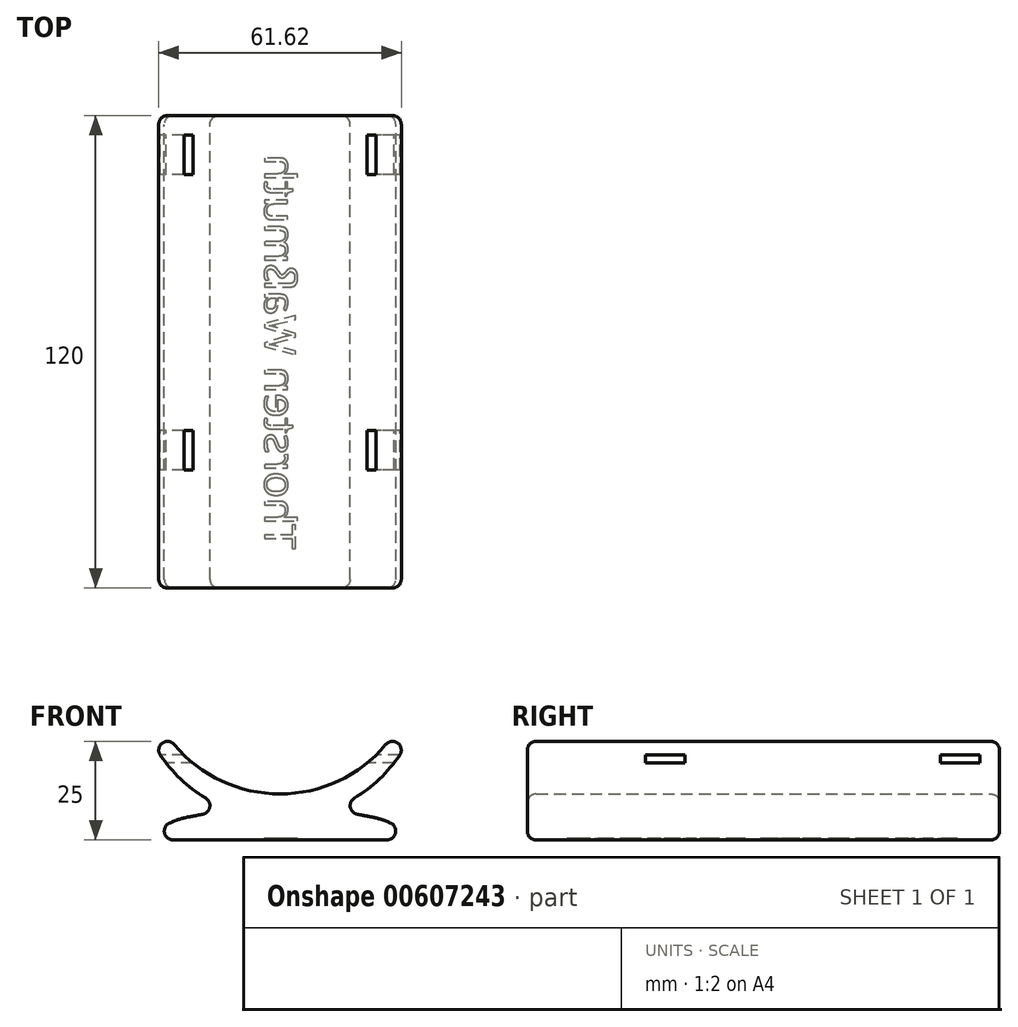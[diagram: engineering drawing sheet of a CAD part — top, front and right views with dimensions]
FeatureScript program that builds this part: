
annotation { "Feature Type Name" : "Feature", "Feature Type Description" : "" }
export const myFeature = defineFeature(function(context is Context, id is Id, definition is map)
    precondition{}
    {
        {
            var Q0;
            Q0=qCreatedBy(makeId("Front.planeOp"),FACE);
            var sketch = newSketch(context, id + "F0", { "sketchPlane" : qUnion([Q0])});
            skLineSegment(sketch, "E0", {"start": v(-32.5, 0) * mm, "end": v(32.5, 0) * mm});
            skLineSegment(sketch, "E1", {"start": v(32.5, 25) * mm, "end": v(27.5, 25) * mm});
            skLineSegment(sketch, "E2", {"start": v(-32.5, 25) * mm, "end": v(-27.5, 25) * mm});
            skArc(sketch, "E3", {"start": v(-27.5, 25) * mm, "mid": v(0, 11.65) * mm, "end": v(27.5, 25) * mm});
            skArc(sketch, "E4", {"start": v(-32.5, 25) * mm, "mid": v(0, 5.37) * mm, "end": v(32.5, 25) * mm});
            skFitSpline(sketch, "E5", {"points": [v(-32.5, 0) * mm, v(-24.4, 5.56) * mm, v(-15.17, 8.65) * mm], "startDerivative": vector(7.79, 17.92) * mm, "endDerivative": vector(11.83, 13.14) * mm});
            skFitSpline(sketch, "E6.MirrorCS", {"points": [v(32.5, 0) * mm, v(24.4, 5.56) * mm, v(15.17, 8.65) * mm], "startDerivative": vector(-7.79, 17.92) * mm, "endDerivative": vector(-11.83, 13.14) * mm});
            skLineSegment(sketch, "E7", {"start": v(15.17, 8.65) * mm, "end": v(-15.17, 8.65) * mm});
            skSolve(sketch);
        }
        {
            var Q0;
            Q0 = qSketchRegion(id + "F0", true);
            extrude(context, id + "F1", {"entities" : qUnion([Q0]), "depth" : 60 * mm, "offsetDistance" : 25 * mm, "hasSecondDirection" : true, "secondDirectionOppositeDirection" : true, "secondDirectionDepth" : 60 * mm});
        }
        {
            var Q0;
            Q0=makeQuery(id+"F1.opExtrude","CAP_EDGE",EDGE,{"disambiguationData":[OSD([sQuery(id+"F0.wireOp",EDGE,"E1")])],"isStart":false});
            var Q1;
            Q1=makeQuery(id+"F1.opExtrude","CAP_EDGE",EDGE,{"disambiguationData":[OSD([sQuery(id+"F0.wireOp",EDGE,"E2")])],"isStart":false});
            var Q2;
            Q2=makeQuery(id+"F1.opExtrude","CAP_EDGE",EDGE,{"disambiguationData":[OSD([sQuery(id+"F0.wireOp",EDGE,"6ac28e1d-b41e-4c74-82fc-2945b80d29a40.MirrorCS")])],"isStart":false});
            var Q3;
            Q3=makeQuery(id+"F1.opExtrude","CAP_EDGE",EDGE,{"disambiguationData":[OSD([sQuery(id+"F0.wireOp",EDGE,"E3")])],"isStart":false});
            var Q4;
            Q4=makeQuery(id+"F1.opExtrude","SWEPT_FACE",FACE,{"disambiguationData":[OSD([sQuery(id+"F0.wireOp",EDGE,"UTH5XIte-BIU0-CYo0-HlKk-KP9v13hWMDFO")])]});
            var Q5;
            Q5=makeQuery(id+"F1.opExtrude","CAP_EDGE",EDGE,{"disambiguationData":[OSD([sQuery(id+"F0.wireOp",EDGE,"E0")])],"isStart":false});
            var Q6;
            Q6=makeQuery(id+"F1.opExtrude","SWEPT_EDGE",EDGE,{"disambiguationData":[OSD([sQuery(id+"F0.wireOp",EDGE,"E2"),sQuery(id+"F0.wireOp",EDGE,"E3")])]});
            var Q7;
            Q7=makeQuery(id+"F1.opExtrude","SWEPT_EDGE",EDGE,{"disambiguationData":[OSD([sQuery(id+"F0.wireOp",EDGE,"E2"),sQuery(id+"F0.wireOp",EDGE,"6ac28e1d-b41e-4c74-82fc-2945b80d29a40.MirrorCS")])]});
            var Q8;
            Q8=makeQuery(id+"F1.opExtrude","CAP_EDGE",EDGE,{"disambiguationData":[OSD([sQuery(id+"F0.wireOp",EDGE,"6ac28e1d-b41e-4c74-82fc-2945b80d29a40.MirrorCS")])],"isStart":true});
            var Q9;
            Q9=makeQuery(id+"F1.opExtrude","CAP_EDGE",EDGE,{"disambiguationData":[OSD([sQuery(id+"F0.wireOp",EDGE,"E3")])],"isStart":true});
            var Q10;
            Q10=makeQuery(id+"F1.opExtrude","CAP_EDGE",EDGE,{"disambiguationData":[OSD([sQuery(id+"F0.wireOp",EDGE,"E1")])],"isStart":true});
            var Q11;
            Q11=makeQuery(id+"F1.opExtrude","CAP_EDGE",EDGE,{"disambiguationData":[OSD([sQuery(id+"F0.wireOp",EDGE,"E2")])],"isStart":true});
            var Q12;
            Q12=makeQuery(id+"F1.opExtrude","CAP_EDGE",EDGE,{"disambiguationData":[OSD([sQuery(id+"F0.wireOp",EDGE,"E0")])],"isStart":true});
            var Q13;
            Q13=makeQuery(id+"F1.opExtrude","SWEPT_EDGE",EDGE,{"disambiguationData":[OSD([sQuery(id+"F0.wireOp",EDGE,"E0"),sQuery(id+"F0.wireOp",EDGE,"6ac28e1d-b41e-4c74-82fc-2945b80d29a40.MirrorCS")])]});
            var Q14;
            Q14=makeQuery(id+"F1.opExtrude","SWEPT_FACE",FACE,{"disambiguationData":[OSD([sQuery(id+"F0.wireOp",EDGE,"E3")])]});
            var Q15;
            {var subQ0=sQuery(id+"F0.wireOp",EDGE,"E4");Q15=makeQuery(id+"F1.opExtrude","CAP_EDGE",EDGE,{"disambiguationData":[OSD([subQ0]),TDD([makeQuery(id+"F0.imprint","IMPRINT",EDGE,{"disambiguationData":[TD([[makeQuery(id+"F0.imprint","INTERSECT",VERTEX,{"derivedFrom":[sQuery(id+"F0.wireOp",EDGE,"E1"),subQ0]}),1.0]])],"derivedFrom":subQ0})])],"isStart":true});}
            var Q16;
            Q16=makeQuery(id+"F1.opExtrude","SWEPT_EDGE",EDGE,{"disambiguationData":[OSD([sQuery(id+"F0.wireOp",EDGE,"E1"),sQuery(id+"F0.wireOp",EDGE,"E4")])]});
            var Q17;
            Q17=makeQuery(id+"F1.opExtrude","CAP_EDGE",EDGE,{"disambiguationData":[OSD([sQuery(id+"F0.wireOp",EDGE,"E6.MirrorCS")])],"isStart":true});
            var Q18;
            {var subQ0=sQuery(id+"F0.wireOp",EDGE,"E4");Q18=makeQuery(id+"F1.opExtrude","CAP_EDGE",EDGE,{"disambiguationData":[OSD([subQ0]),TDD([makeQuery(id+"F0.imprint","IMPRINT",EDGE,{"disambiguationData":[TD([[makeQuery(id+"F0.imprint","INTERSECT",VERTEX,{"derivedFrom":[sQuery(id+"F0.wireOp",EDGE,"E2"),subQ0]}),-1.0]])],"derivedFrom":subQ0})])],"isStart":true});}
            var Q19;
            Q19=makeQuery(id+"F1.opExtrude","CAP_EDGE",EDGE,{"disambiguationData":[OSD([sQuery(id+"F0.wireOp",EDGE,"E5")])],"isStart":true});
            var Q20;
            {var subQ0=sQuery(id+"F0.wireOp",EDGE,"E4");Q20=makeQuery(id+"F1.opExtrude","CAP_EDGE",EDGE,{"disambiguationData":[OSD([subQ0]),TDD([makeQuery(id+"F0.imprint","IMPRINT",EDGE,{"disambiguationData":[TD([[makeQuery(id+"F0.imprint","INTERSECT",VERTEX,{"derivedFrom":[sQuery(id+"F0.wireOp",EDGE,"E2"),subQ0]}),-1.0]])],"derivedFrom":subQ0})])],"isStart":false});}
            var Q21;
            Q21=makeQuery(id+"F1.opExtrude","CAP_EDGE",EDGE,{"disambiguationData":[OSD([sQuery(id+"F0.wireOp",EDGE,"E5")])],"isStart":false});
            var Q22;
            Q22=makeQuery(id+"F1.opExtrude","CAP_EDGE",EDGE,{"disambiguationData":[OSD([sQuery(id+"F0.wireOp",EDGE,"E6.MirrorCS")])],"isStart":false});
            var Q23;
            {var subQ0=sQuery(id+"F0.wireOp",EDGE,"E4");Q23=makeQuery(id+"F1.opExtrude","CAP_EDGE",EDGE,{"disambiguationData":[OSD([subQ0]),TDD([makeQuery(id+"F0.imprint","IMPRINT",EDGE,{"disambiguationData":[TD([[makeQuery(id+"F0.imprint","INTERSECT",VERTEX,{"derivedFrom":[sQuery(id+"F0.wireOp",EDGE,"E1"),subQ0]}),1.0]])],"derivedFrom":subQ0})])],"isStart":false});}
            var Q24;
            Q24=makeQuery(id+"F1.opExtrude","SWEPT_EDGE",EDGE,{"disambiguationData":[OSD([sQuery(id+"F0.wireOp",EDGE,"E4"),sQuery(id+"F0.wireOp",EDGE,"E6.MirrorCS")])]});
            var Q25;
            Q25=makeQuery(id+"F1.opExtrude","SWEPT_EDGE",EDGE,{"disambiguationData":[OSD([sQuery(id+"F0.wireOp",EDGE,"E4"),sQuery(id+"F0.wireOp",EDGE,"E5")])]});
            fillet(context, id + "F2", {"entities" : qUnion([Q0, Q1, Q2, Q3, Q4, Q5, Q6, Q7, Q8, Q9, Q10, Q11, Q12, Q13, Q14, Q15, Q16, Q17, Q18, Q19, Q20, Q21, Q22, Q23, Q24, Q25]), "radius" : 2.22 * mm, "tangentPropagation" : true, "allowEdgeOverflow" : false});
        }
        {
            var Q0;
            Q0=qCreatedBy(makeId("Right.planeOp"),FACE);
            var sketch = newSketch(context, id + "F3", { "sketchPlane" : qUnion([Q0])});
            skLineSegment(sketch, "E8.bottom", {"start": v(45, 21.54) * mm, "end": v(55, 21.54) * mm});
            skLineSegment(sketch, "E8.top", {"start": v(45, 19.54) * mm, "end": v(55, 19.54) * mm});
            skLineSegment(sketch, "E8.left", {"start": v(45, 21.54) * mm, "end": v(45, 19.54) * mm});
            skLineSegment(sketch, "E8.right", {"start": v(55, 21.54) * mm, "end": v(55, 19.54) * mm});
            skLineSegment(sketch, "E9.bottom", {"start": v(-30, 21.54) * mm, "end": v(-20, 21.54) * mm});
            skLineSegment(sketch, "E9.top", {"start": v(-30, 19.54) * mm, "end": v(-20, 19.54) * mm});
            skLineSegment(sketch, "E9.left", {"start": v(-30, 21.54) * mm, "end": v(-30, 19.54) * mm});
            skLineSegment(sketch, "E9.right", {"start": v(-20, 21.54) * mm, "end": v(-20, 19.54) * mm});
            skSolve(sketch);
        }
        {
            var Q0;
            Q0=qSketchRegion(id+"F3",true);
            extrude(context, id + "F4", {"entities" : qUnion([Q0]), "operationType" : NewBodyOperationType.REMOVE, "endBound" : BoundingType.THROUGH_ALL, "depth" : 25 * mm, "offsetDistance" : 25 * mm, "hasSecondDirection" : true, "secondDirectionBound" : SecondDirectionBoundingType.THROUGH_ALL, "secondDirectionOppositeDirection" : true, "secondDirectionDepth" : 25 * mm});
        }
        {
            var Q0;
            Q0=makeQuery(id+"F1.opExtrude","SWEPT_FACE",FACE,{"disambiguationData":[OSD([sQuery(id+"F0.wireOp",EDGE,"E0")])]});
            var sketch = newSketch(context, id + "F5", { "sketchPlane" : qUnion([Q0])});
            skText(sketch, "E10", { "text": "Thorsten Waßmuth", "fontName": "OpenSans-Regular.ttf"});
            const initialGuessF5  = {"E10": [-0.00398, 0.05, 0, -1, 0.00796]};
            skSetInitialGuess(sketch, initialGuessF5);
            skSolve(sketch);
        }
        {
            var Q0;
            Q0 = qSketchRegion(id + "F5", true);
            extrude(context, id + "F6", {"entities" : qUnion([Q0]), "operationType" : NewBodyOperationType.REMOVE, "depth" : -0.4 * mm, "offsetDistance" : 25 * mm});
        }
    });
